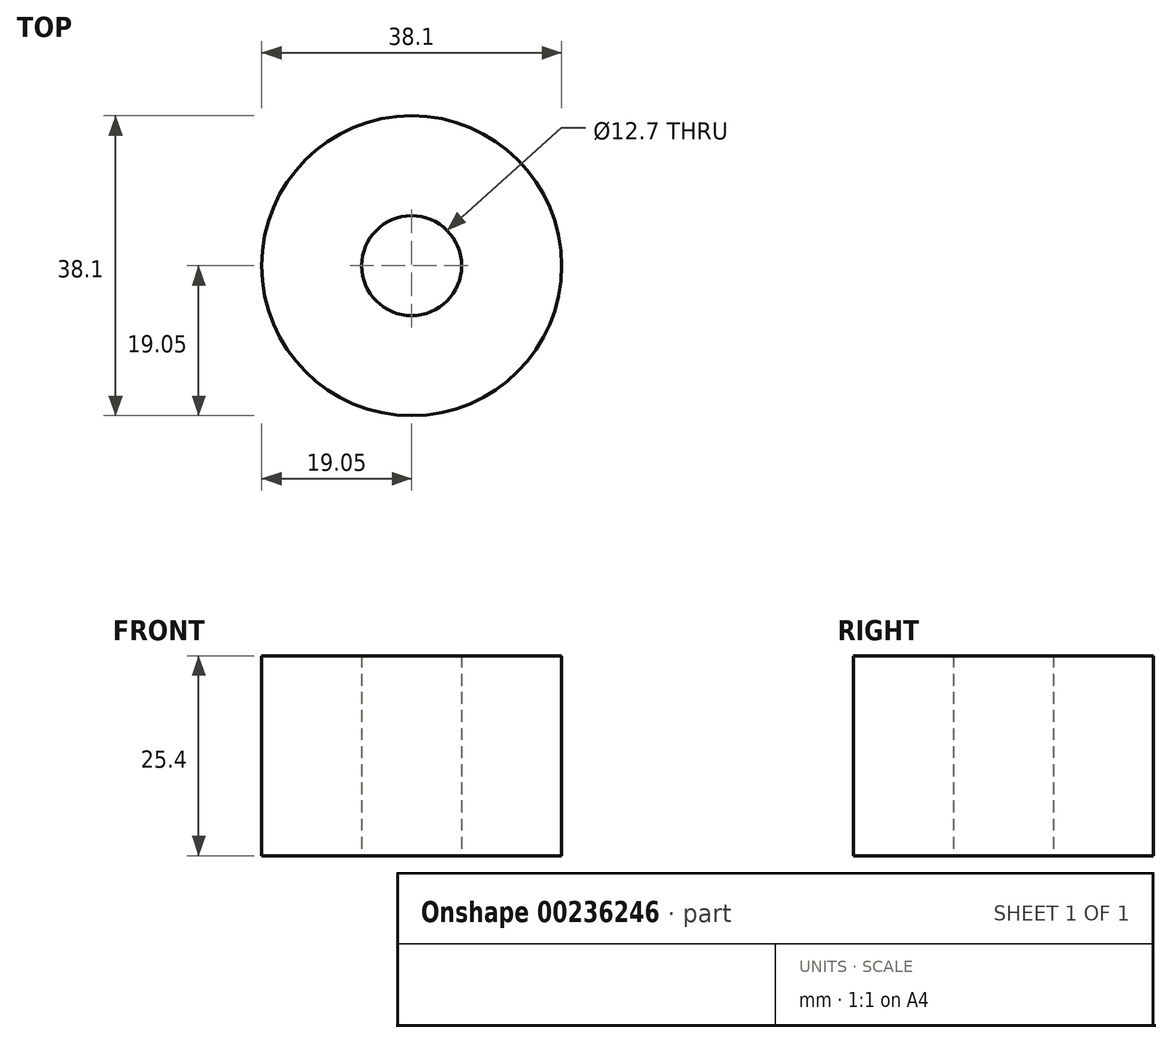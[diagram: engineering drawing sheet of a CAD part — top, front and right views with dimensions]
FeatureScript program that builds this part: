
annotation { "Feature Type Name" : "Feature", "Feature Type Description" : "" }
export const myFeature = defineFeature(function(context is Context, id is Id, definition is map)
    precondition{}
    {
        {
            var Q0;
            Q0=qCreatedBy(makeId("Top.planeOp"),FACE);
            var sketch = newSketch(context, id + "F0", { "sketchPlane" : qUnion([Q0])});
            skCircle(sketch, "E0", {"center": v(0, 0) * mm, "radius": 19.05 * mm});
            skCircle(sketch, "E1", {"center": v(0, 0) * mm, "radius": 6.35 * mm});
            skSolve(sketch);
        }
        {
            var Q0;
            Q0 = qSketchRegion(id + "F0", true);
            extrude(context, id + "F1", {"entities" : qUnion([Q0]), "endBound" : BoundingType.SYMMETRIC, "depth" : 25.4 * mm});
        }
    });
